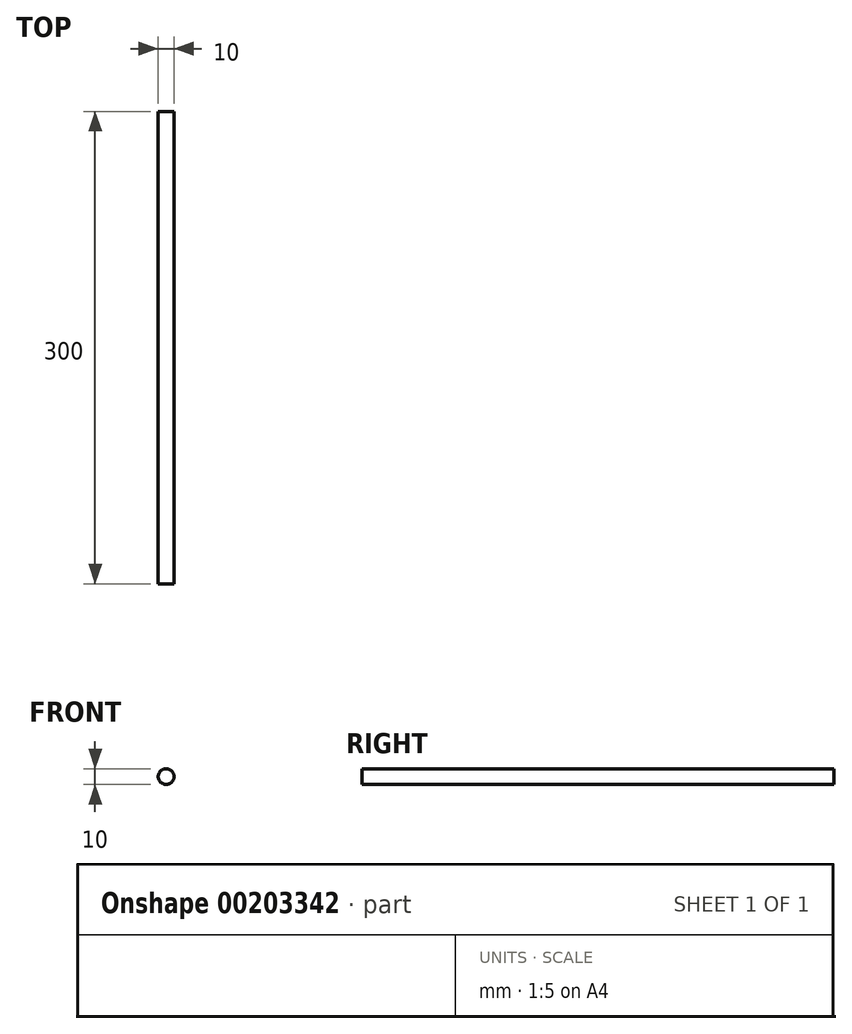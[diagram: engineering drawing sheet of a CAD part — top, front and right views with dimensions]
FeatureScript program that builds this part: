
annotation { "Feature Type Name" : "Feature", "Feature Type Description" : "" }
export const myFeature = defineFeature(function(context is Context, id is Id, definition is map)
    precondition{}
    {
        {
            var Q0;
            Q0=qCreatedBy(makeId("Front.planeOp"),FACE);
            var sketch = newSketch(context, id + "F0", { "sketchPlane" : qUnion([Q0])});
            skCircle(sketch, "E0", {"center": v(0, 0) * mm, "radius": 5 * mm});
            skSolve(sketch);
        }
        {
            var Q0;
            Q0=makeQuery(id+"F0.imprint","IMPRINT",FACE,{"disambiguationData":[TD([[makeQuery(id+"F0.imprint","IMPRINT",EDGE,{"derivedFrom":sQuery(id+"F0.wireOp",EDGE,"E0")}),1.0]])]});
            extrude(context, id + "F1", {"entities" : qUnion([Q0]), "depth" : 300 * mm});
        }
    });
